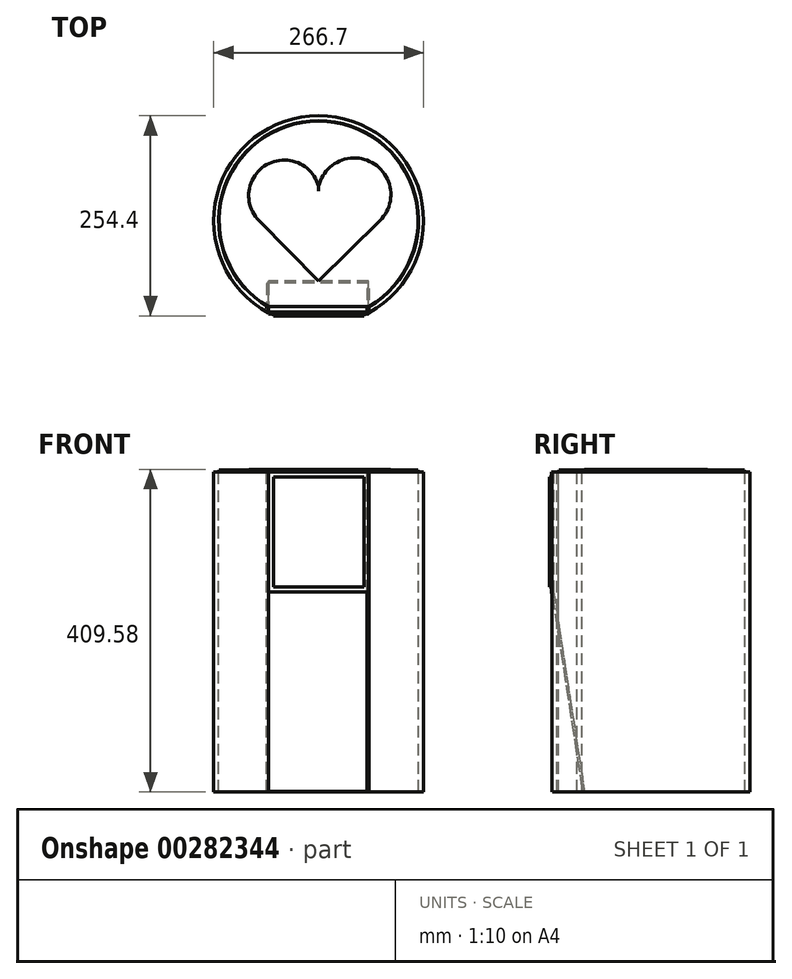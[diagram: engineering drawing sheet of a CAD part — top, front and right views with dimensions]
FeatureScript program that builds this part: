
annotation { "Feature Type Name" : "Feature", "Feature Type Description" : "" }
export const myFeature = defineFeature(function(context is Context, id is Id, definition is map)
    precondition{}
    {
        {
            var Q0;
            Q0=qCreatedBy(makeId("Top.planeOp"),FACE);
            var sketch = newSketch(context, id + "F0", { "sketchPlane" : qUnion([Q0])});
            skArc(sketch, "E0", {"start": v(63.64, -109.9) * mm, "mid": v(-0.12, 127) * mm, "end": v(-63.43, -110.03) * mm});
            skArc(sketch, "E1.0", {"start": v(63.64, -117.18) * mm, "mid": v(-0.13, 133.35) * mm, "end": v(-63.42, -117.3) * mm});
            skLineSegment(sketch, "E2", {"start": v(-63.43, -110.03) * mm, "end": v(63.64, -109.9) * mm});
            skLineSegment(sketch, "E3", {"start": v(63.64, -109.9) * mm, "end": v(63.64, -117.18) * mm});
            skLineSegment(sketch, "E4", {"start": v(-63.43, -110.03) * mm, "end": v(-63.42, -117.3) * mm});
            skLineSegment(sketch, "E5", {"start": v(-63.42, -117.3) * mm, "end": v(63.64, -117.18) * mm});
            skSolve(sketch);
        }
        {
            var Q0;
            Q0=makeQuery(id+"F0.imprint","IMPRINT",FACE,{"disambiguationData":[TD([[makeQuery(id+"F0.imprint","IMPRINT",EDGE,{"derivedFrom":sQuery(id+"F0.wireOp",EDGE,"E0")}),-1.0]])]});
            extrude(context, id + "F1", {"entities" : qUnion([Q0]), "oppositeDirection" : true, "depth" : 406.4 * mm});
        }
        {
            var Q0;
            Q0=qCreatedBy(makeId("Top.planeOp"),FACE);
            var sketch = newSketch(context, id + "F2", { "sketchPlane" : qUnion([Q0])});
            skArc(sketch, "E6", {"start": v(63.88, -109.03) * mm, "mid": v(0, 126.37) * mm, "end": v(-63.88, -109.03) * mm});
            skLineSegment(sketch, "E7", {"start": v(-63.88, -109.03) * mm, "end": v(63.88, -109.03) * mm});
            skSolve(sketch);
        }
        {
            var Q0;
            Q0 = qSketchRegion(id + "F2", true);
            extrude(context, id + "F3", {"entities" : qUnion([Q0]), "depth" : 2.54 * mm});
        }
        {
            var Q0;
            Q0=makeQuery(id+"F3.opExtrude","CAP_FACE",FACE,{"disambiguationData":[OSD([sQuery(id+"F2.wireOp",EDGE,"E6")])],"isStart":false});
            var sketch = newSketch(context, id + "F4", { "sketchPlane" : qUnion([Q0])});
            skLineSegment(sketch, "E8", {"start": v(-75.8, 0) * mm, "end": v(0, -76.85) * mm});
            skLineSegment(sketch, "E9", {"start": v(0, -76.85) * mm, "end": v(77.92, 0) * mm});
            skArc(sketch, "E10", {"start": v(0, 43.69) * mm, "mid": v(-66.19, 70.92) * mm, "end": v(-75.8, 0) * mm});
            skArc(sketch, "E11", {"start": v(77.92, 0) * mm, "mid": v(68, 73.65) * mm, "end": v(0, 43.69) * mm});
            skSolve(sketch);
        }
        {
            var Q0;
            Q0 = qSketchRegion(id + "F4", true);
            extrude(context, id + "F5", {"entities" : qUnion([Q0]), "operationType" : NewBodyOperationType.ADD, "depth" : 0.64 * mm});
        }
        {
            var Q0;
            Q0=makeQuery(id+"F5.opExtrude","CAP_EDGE",EDGE,{"disambiguationData":[OSD([sQuery(id+"F4.wireOp",EDGE,"E9")])],"isStart":false});
            var Q1;
            Q1=makeQuery(id+"F5.opExtrude","CAP_EDGE",EDGE,{"disambiguationData":[OSD([sQuery(id+"F4.wireOp",EDGE,"E11")])],"isStart":false});
            var Q2;
            Q2=makeQuery(id+"F5.opExtrude","CAP_EDGE",EDGE,{"disambiguationData":[OSD([sQuery(id+"F4.wireOp",EDGE,"E10")])],"isStart":false});
            var Q3;
            Q3=makeQuery(id+"F5.opExtrude","CAP_EDGE",EDGE,{"disambiguationData":[OSD([sQuery(id+"F4.wireOp",EDGE,"E8")])],"isStart":false});
            fillet(context, id + "F6", {"entities" : qUnion([Q0, Q1, Q2, Q3]), "radius" : 1.27 * mm, "tangentPropagation" : true, "allowEdgeOverflow" : false});
        }
        {
            var Q0;
            Q0=qCreatedBy(makeId("Right.planeOp"),FACE);
            var sketch = newSketch(context, id + "F7", { "sketchPlane" : qUnion([Q0])});
            skLineSegment(sketch, "E12", {"start": v(-118.51, -152.4) * mm, "end": v(-79.2, -406.08) * mm});
            skLineSegment(sketch, "E13.0", {"start": v(-116, -152.02) * mm, "end": v(-76.7, -405.7) * mm});
            skLineSegment(sketch, "E14", {"start": v(-79.2, -406.08) * mm, "end": v(-76.7, -405.7) * mm});
            skLineSegment(sketch, "E15", {"start": v(-118.51, -152.4) * mm, "end": v(-118.51, 0) * mm});
            skLineSegment(sketch, "E16", {"start": v(-118.51, 0) * mm, "end": v(-115.97, 0) * mm});
            skLineSegment(sketch, "E17", {"start": v(-115.97, 0) * mm, "end": v(-116, -152.02) * mm});
            skSolve(sketch);
        }
        {
            var Q0;
            Q0 = qSketchRegion(id + "F7", true);
            extrude(context, id + "F8", {"entities" : qUnion([Q0]), "operationType" : NewBodyOperationType.ADD, "endBound" : BoundingType.SYMMETRIC, "depth" : 127 * mm});
        }
        {
            var Q0;
            Q0=makeQuery(id+"F3.opExtrude","CAP_FACE",FACE,{"disambiguationData":[OSD([sQuery(id+"F2.wireOp",EDGE,"E6")])],"isStart":true});
            var sketch = newSketch(context, id + "F9", { "sketchPlane" : qUnion([Q0])});
            skLineSegment(sketch, "E18.bottom", {"start": v(-63.8, 79.79) * mm, "end": v(-66.34, 79.79) * mm});
            skLineSegment(sketch, "E18.top", {"start": v(-63.8, 111.54) * mm, "end": v(-66.34, 111.54) * mm});
            skLineSegment(sketch, "E18.left", {"start": v(-63.8, 79.79) * mm, "end": v(-63.8, 111.54) * mm});
            skLineSegment(sketch, "E18.right", {"start": v(-66.34, 79.79) * mm, "end": v(-66.34, 111.54) * mm});
            skLineSegment(sketch, "E19.bottom", {"start": v(63.97, 85.97) * mm, "end": v(61.43, 85.97) * mm});
            skLineSegment(sketch, "E19.top", {"start": v(63.97, 117.72) * mm, "end": v(61.43, 117.72) * mm});
            skLineSegment(sketch, "E19.left", {"start": v(63.97, 85.97) * mm, "end": v(63.97, 117.72) * mm});
            skLineSegment(sketch, "E19.right", {"start": v(61.43, 85.97) * mm, "end": v(61.43, 117.72) * mm});
            skSolve(sketch);
        }
        {
            var Q0;
            Q0 = qSketchRegion(id + "F9", true);
            extrude(context, id + "F10", {"entities" : qUnion([Q0]), "depth" : 406.4 * mm});
        }
        {
            var Q0;
            Q0=makeQuery(id+"F8.opExtrude","SWEPT_FACE",FACE,{"disambiguationData":[OSD([sQuery(id+"F7.wireOp",EDGE,"E15")])]});
            var sketch = newSketch(context, id + "F11", { "sketchPlane" : qUnion([Q0])});
            skLineSegment(sketch, "E20.bottom", {"start": v(-57.15, -6.35) * mm, "end": v(57.62, -6.35) * mm});
            skLineSegment(sketch, "E20.top", {"start": v(-57.15, -146.05) * mm, "end": v(57.62, -146.05) * mm});
            skLineSegment(sketch, "E20.left", {"start": v(-57.15, -6.35) * mm, "end": v(-57.15, -146.05) * mm});
            skLineSegment(sketch, "E20.right", {"start": v(57.62, -6.35) * mm, "end": v(57.62, -146.05) * mm});
            skSolve(sketch);
        }
        {
            var Q0;
            Q0 = qSketchRegion(id + "F11", true);
            extrude(context, id + "F12", {"entities" : qUnion([Q0]), "operationType" : NewBodyOperationType.ADD, "depth" : 2.54 * mm});
        }
    });
